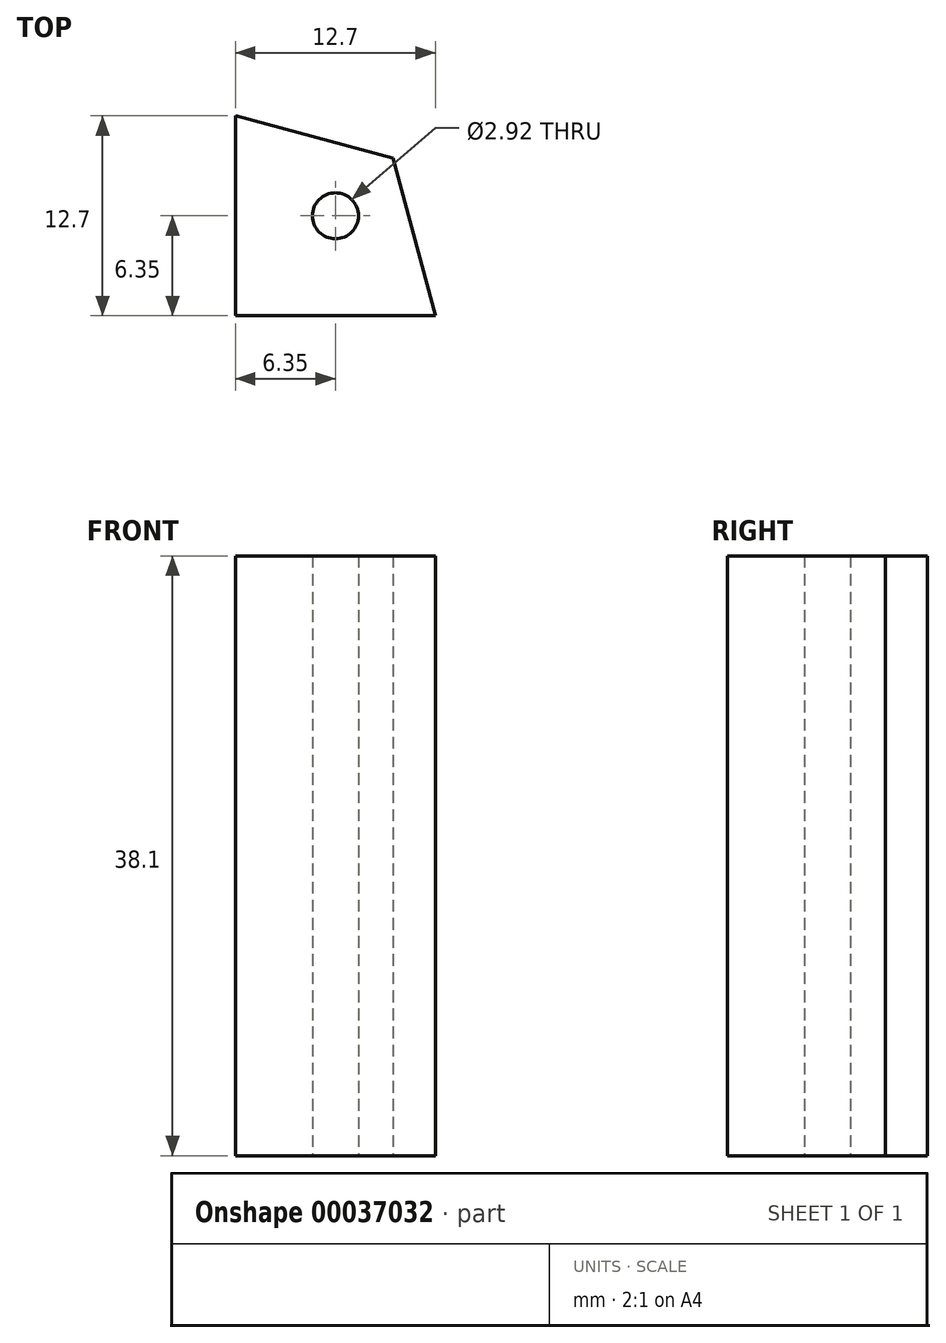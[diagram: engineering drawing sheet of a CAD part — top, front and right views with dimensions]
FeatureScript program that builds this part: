
annotation { "Feature Type Name" : "Feature", "Feature Type Description" : "" }
export const myFeature = defineFeature(function(context is Context, id is Id, definition is map)
    precondition{}
    {
        {
            var Q0;
            Q0=qCreatedBy(makeId("Top.planeOp"),FACE);
            var sketch = newSketch(context, id + "F0", { "sketchPlane" : qUnion([Q0])});
            skLineSegment(sketch, "E0.rect.bottom", {"start": v(6.35, 6.35) * mm, "end": v(-6.35, 6.35) * mm, "construction": true});
            skLineSegment(sketch, "E0.rect.top", {"start": v(6.35, -6.35) * mm, "end": v(-6.35, -6.35) * mm});
            skLineSegment(sketch, "E0.rect.left", {"start": v(6.35, 6.35) * mm, "end": v(6.35, -6.35) * mm, "construction": true});
            skLineSegment(sketch, "E0.rect.right", {"start": v(-6.35, 6.35) * mm, "end": v(-6.35, -6.35) * mm});
            skPoint(sketch, "E0.rect.middle", {"position": v(0, 0) * mm});
            skLineSegment(sketch, "E1", {"start": v(-6.35, 6.35) * mm, "end": v(3.67, 3.67) * mm});
            skLineSegment(sketch, "E2", {"start": v(3.67, 3.67) * mm, "end": v(6.35, -6.35) * mm});
            skLineSegment(sketch, "E3", {"start": v(-6.35, -6.35) * mm, "end": v(6.35, 6.35) * mm, "construction": true});
            skCircle(sketch, "E4", {"center": v(0, 0) * mm, "radius": 1.46 * mm});
            skSolve(sketch);
        }
        {
            var Q0;
            Q0=makeQuery(id+"F0.imprint","IMPRINT",FACE,{"disambiguationData":[TD([[makeQuery(id+"F0.imprint","IMPRINT",EDGE,{"derivedFrom":sQuery(id+"F0.wireOp",EDGE,"E0.rect.top")}),-1.0]])]});
            extrude(context, id + "F1", {"entities" : qUnion([Q0]), "endBound" : BoundingType.SYMMETRIC, "depth" : 38.1 * mm});
        }
    });
